# Revit family: ITK_Лицевая рамка для модуля Mosaic 80х80_IP20
name_source: partatom
category: Обобщенные модели
units: mm (PartAtom-declared; Revit-internal decimal feet)

## family parameters
Всегда вертикально = Да
Может служить основой для арматурных стержней = Нет
На основе рабочей плоскости = Нет
Общий = Нет
При загрузке вырезать с полостями = Нет
Размер круглого соединителя = Использовать диаметр
Тип детали = Нормальный
Точка расчета площади = Нет

## types (2) — shared parameters
ADSK_URL страницы изделия = https://www.itk-group.ru
ADSK_Версия Revit = 2019
ADSK_Версия семейства = 1.0
ADSK_Группирование = I. ЩИТЫ И ПУЛЬТЫ
ADSK_Единица измерения = шт
ADSK_Завод-изготовитель = IEK
IEK_URL = https://www.itk-group.ru
IEK_Описание = Изготовлены из высококачественных негорючих материалов.
Надежность и удобство эксплуатации.
Соответствие международным стандартам качества.
KSI_CMa_Строительные материалы = 01.7.14.03
URL = https://www.iek.ru
Высота = 80 мм
Изготовитель = ITK
Степень защиты = IP20
Ширина = 80 мм

## per-type parameters (varying)
| type | ADSK_Код изделия | ADSK_Масса | ADSK_Материал наименование | ADSK_Наименование | IEK_Цена за единицу | Глубина | Материал | Пластиковый суппорт |
| Металлический суппорт | CS5-12M-M | 0.034 | Пластик/металл | ITK Лицевая рамка для мод. Mosaic 80х80мм мет. суппорт бел. | 103.38 | 13 мм | Нержавеющая сталь | Да |
| Пластиковый суппорт | CS5-12M-P | 0.028 | Пластик | ITK Лицевая рамка для мод. Mosaic 80х80мм пл. суппорт бел. | 77.38 | 9 мм | Пластик белый | Нет |
